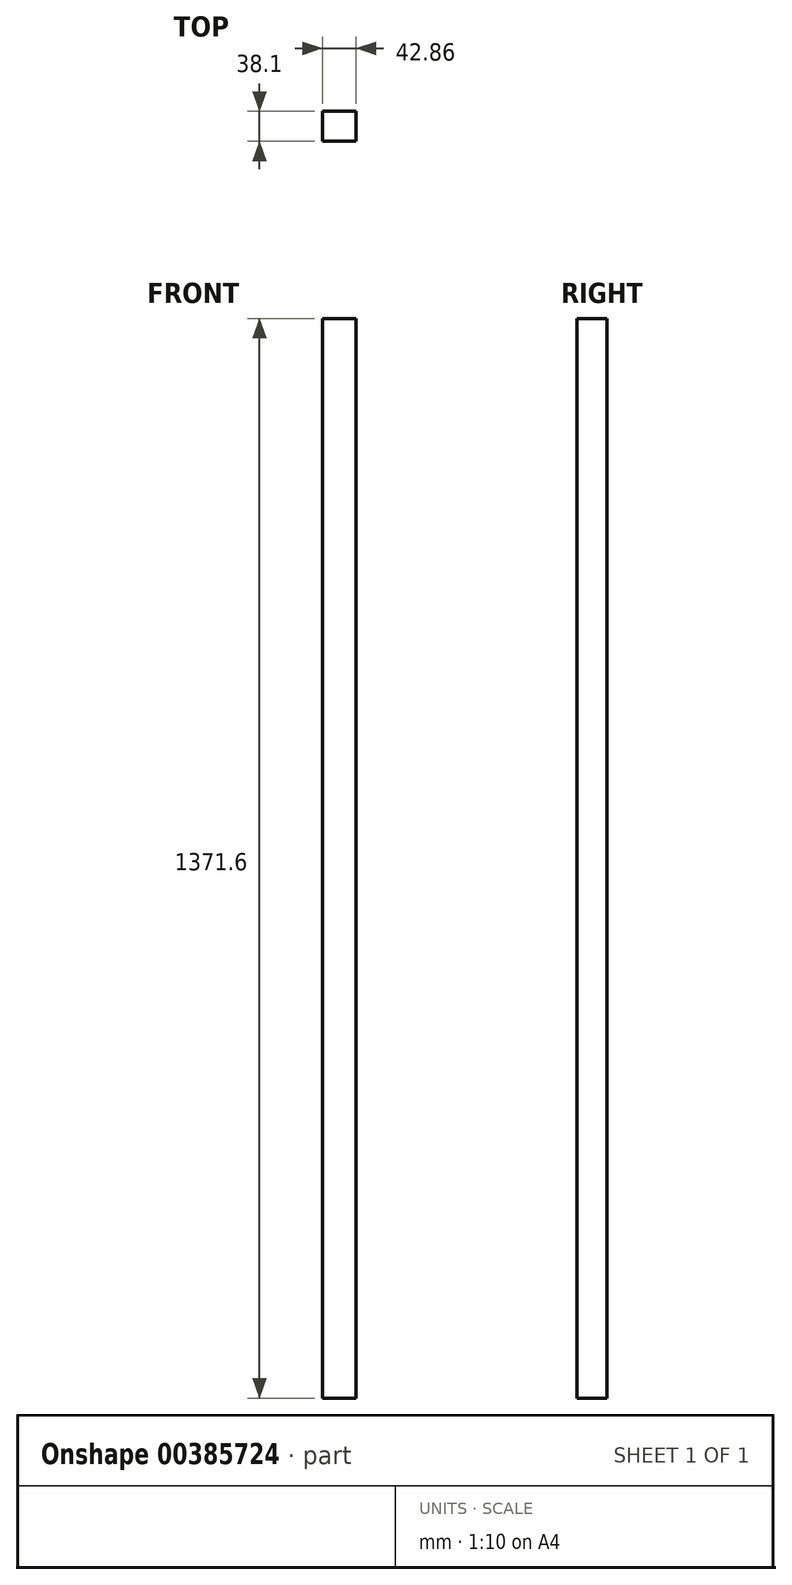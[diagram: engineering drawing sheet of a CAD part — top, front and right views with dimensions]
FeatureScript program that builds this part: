
annotation { "Feature Type Name" : "Feature", "Feature Type Description" : "" }
export const myFeature = defineFeature(function(context is Context, id is Id, definition is map)
    precondition{}
    {
        {
            var Q0;
            Q0=qCreatedBy(makeId("Top.planeOp"),FACE);
            var sketch = newSketch(context, id + "F0", { "sketchPlane" : qUnion([Q0])});
            skLineSegment(sketch, "E0.bottom", {"start": v(21.43, -19.05) * mm, "end": v(-21.43, -19.05) * mm});
            skLineSegment(sketch, "E0.top", {"start": v(21.43, 19.05) * mm, "end": v(-21.43, 19.05) * mm});
            skLineSegment(sketch, "E0.left", {"start": v(21.43, -19.05) * mm, "end": v(21.43, 19.05) * mm});
            skLineSegment(sketch, "E0.right", {"start": v(-21.43, -19.05) * mm, "end": v(-21.43, 19.05) * mm});
            skPoint(sketch, "E0.middle", {"position": v(0, 0) * mm});
            skSolve(sketch);
        }
        {
            var Q0;
            Q0=makeQuery(id+"F0.imprint","IMPRINT",FACE,{"disambiguationData":[TD([[makeQuery(id+"F0.imprint","IMPRINT",EDGE,{"derivedFrom":sQuery(id+"F0.wireOp",EDGE,"E0.bottom")}),-1.0]])]});
            extrude(context, id + "F1", {"entities" : qUnion([Q0]), "depth" : 1371.6 * mm});
        }
    });
